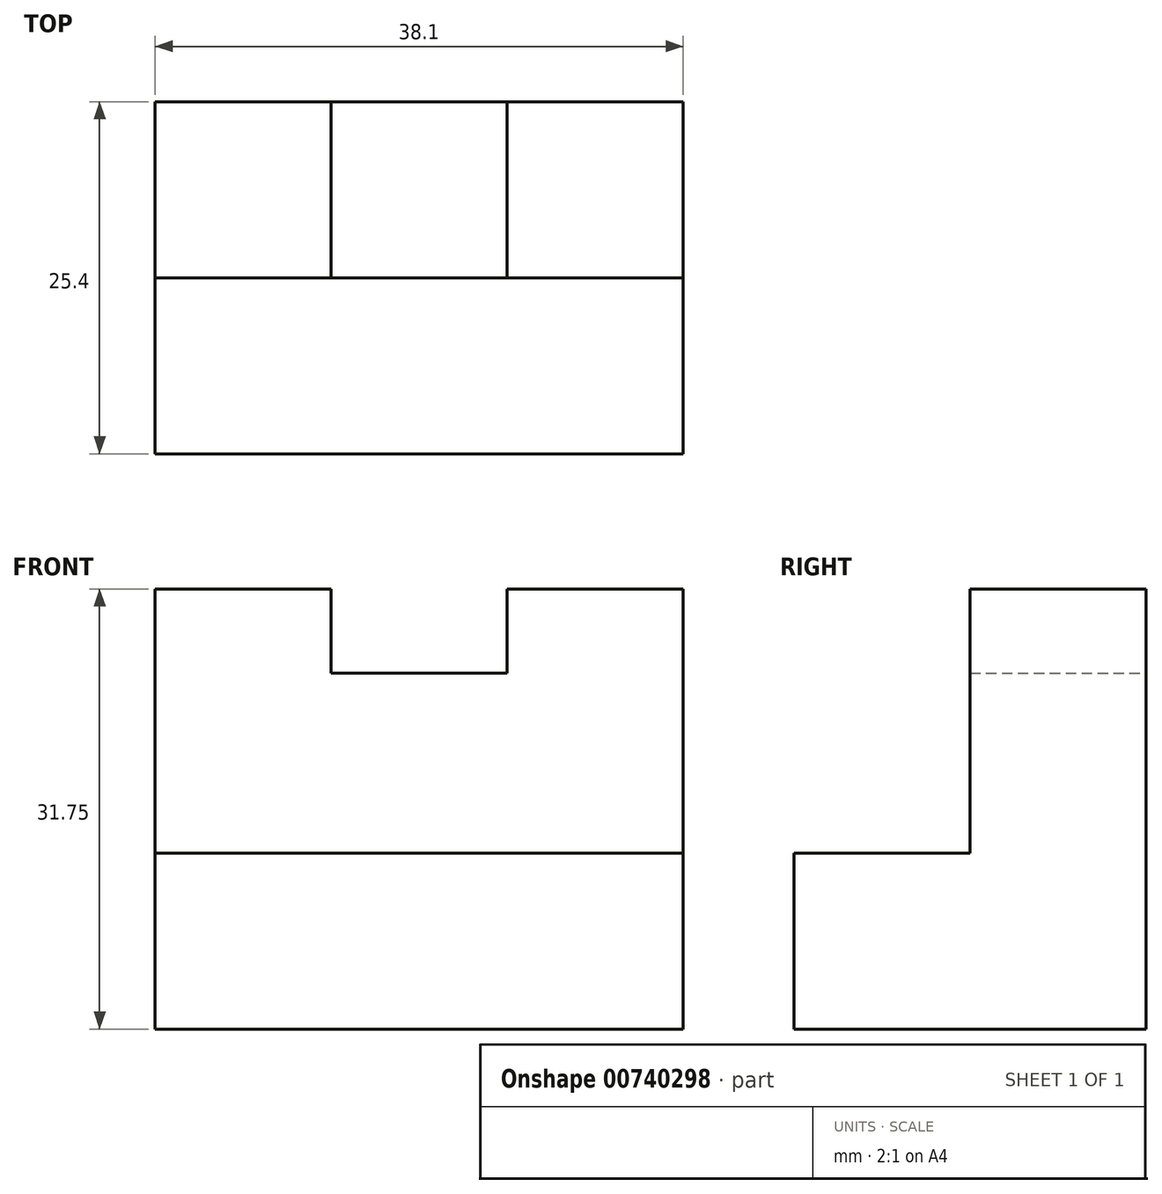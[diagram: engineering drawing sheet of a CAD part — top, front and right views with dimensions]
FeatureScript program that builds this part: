
annotation { "Feature Type Name" : "Feature", "Feature Type Description" : "" }
export const myFeature = defineFeature(function(context is Context, id is Id, definition is map)
    precondition{}
    {
        {
            var Q0;
            Q0=qCreatedBy(makeId("Right.planeOp"),FACE);
            var sketch = newSketch(context, id + "F0", { "sketchPlane" : qUnion([Q0])});
            skLineSegment(sketch, "E0", {"start": v(0, 0) * mm, "end": v(-25.4, 0) * mm});
            skLineSegment(sketch, "E1", {"start": v(-25.4, 0) * mm, "end": v(-25.4, 12.7) * mm});
            skLineSegment(sketch, "E2", {"start": v(-25.4, 12.7) * mm, "end": v(-12.7, 12.7) * mm});
            skLineSegment(sketch, "E3", {"start": v(-12.7, 12.7) * mm, "end": v(-12.7, 31.75) * mm});
            skLineSegment(sketch, "E4", {"start": v(-12.7, 31.75) * mm, "end": v(0, 31.75) * mm});
            skLineSegment(sketch, "E5", {"start": v(0, 31.75) * mm, "end": v(0, 0) * mm});
            skSolve(sketch);
        }
        {
            var Q0;
            Q0 = qSketchRegion(id + "F0", true);
            var Q1;
            Q1 = qSketchRegion(id + "FdqXJYIyHaVaeze_1", true);
            extrude(context, id + "F1", {"entities" : qUnion([Q0, Q1]), "depth" : 38.1 * mm, "offsetDistance" : 25.4 * mm});
        }
        {
            var Q0;
            Q0=qCreatedBy(makeId("Top.planeOp"),FACE);
            var sketch = newSketch(context, id + "F2", { "sketchPlane" : qUnion([Q0])});
            skLineSegment(sketch, "E6", {"start": v(12.7, 0) * mm, "end": v(12.7, -12.7) * mm});
            skLineSegment(sketch, "E7", {"start": v(12.7, -12.7) * mm, "end": v(25.4, -12.7) * mm});
            skLineSegment(sketch, "E8", {"start": v(25.4, -12.7) * mm, "end": v(25.4, 0) * mm});
            skLineSegment(sketch, "E9", {"start": v(25.4, 0) * mm, "end": v(12.7, 0) * mm});
            skLineSegment(sketch, "E10", {"start": v(12.7, 0) * mm, "end": v(0, 0) * mm});
            skLineSegment(sketch, "E11", {"start": v(0, 0) * mm, "end": v(0, -12.57) * mm});
            skLineSegment(sketch, "E12", {"start": v(0, -12.57) * mm, "end": v(12.7, -12.7) * mm});
            skLineSegment(sketch, "E13", {"start": v(25.4, -12.7) * mm, "end": v(38.1, -12.83) * mm});
            skLineSegment(sketch, "E14", {"start": v(38.1, -12.83) * mm, "end": v(38.1, 0) * mm});
            skLineSegment(sketch, "E15", {"start": v(38.1, 0) * mm, "end": v(25.4, 0) * mm});
            skSolve(sketch);
        }
        {
            var Q0;
            Q0=makeQuery(id+"F2.imprint","IMPRINT",FACE,{"disambiguationData":[TD([[makeQuery(id+"F2.imprint","IMPRINT",EDGE,{"derivedFrom":sQuery(id+"F2.wireOp",EDGE,"E6")}),1.0]])]});
            extrude(context, id + "F3", {"entities" : qUnion([Q0]), "operationType" : NewBodyOperationType.ADD, "depth" : 25.4 * mm, "offsetDistance" : 25.4 * mm});
        }
        {
            var Q0;
            Q0=qCreatedBy(makeId("Front.planeOp"),FACE);
            var sketch = newSketch(context, id + "F4", { "sketchPlane" : qUnion([Q0])});
            skLineSegment(sketch, "E16", {"start": v(12.7, 32.02) * mm, "end": v(12.7, 25.67) * mm});
            skLineSegment(sketch, "E17", {"start": v(12.7, 25.67) * mm, "end": v(25.4, 25.67) * mm});
            skLineSegment(sketch, "E18", {"start": v(25.4, 25.67) * mm, "end": v(25.4, 32.02) * mm});
            skLineSegment(sketch, "E19", {"start": v(25.4, 32.02) * mm, "end": v(12.7, 32.02) * mm});
            skSolve(sketch);
        }
        {
            var Q0;
            Q0 = qSketchRegion(id + "F4", true);
            extrude(context, id + "F5", {"entities" : qUnion([Q0]), "operationType" : NewBodyOperationType.REMOVE, "depth" : 25.4 * mm, "offsetDistance" : 25.4 * mm});
        }
    });
